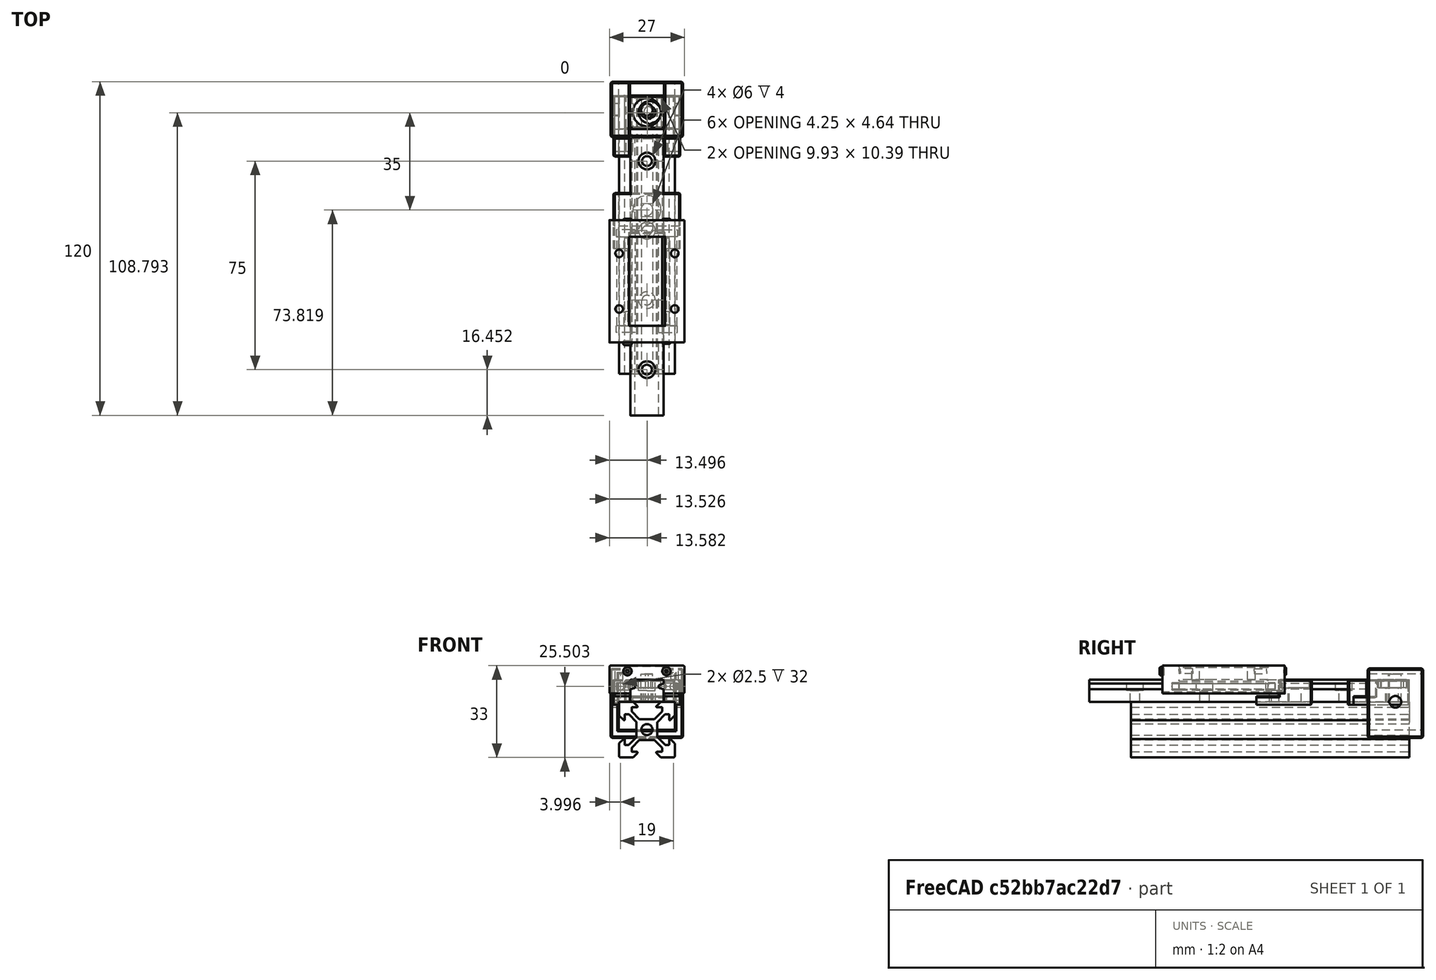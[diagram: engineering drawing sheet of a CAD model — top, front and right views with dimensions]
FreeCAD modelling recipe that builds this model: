
FCSTD DOCUMENT  (FreeCAD 0.18R16146 (Git))
Label: rail-mounter
License: All rights reserved
LicenseURL: http://en.wikipedia.org/wiki/All_rights_reserved
objects: Part::Box×14, Part::Feature×13, Part::Cut×10, Part::Chamfer×8, Part::MultiFuse×8, Part::Cylinder×6
note: 59 computed .brp shape members not serialized (recipe doc carries the construction recipe); baked Part::Feature solids carry a one-line shape summary decoded from their .brp

FEATURE [Part::Box] Box  label="Cube"
  AttacherType = Attacher::AttachEngine3D
  Height = 8
  Length = 24
  Placement = pos=(-12,3,0) rot=(0,0,1;0rad)
  Width = 12
FEATURE [Part::Box] Box001  label="ref"
  AttacherType = Attacher::AttachEngine3D
  Height = 2
  Length = 12.2
  Placement = pos=(-6.1,-5,0) rot=(0,0,1;0rad)
  Width = 4.5
FEATURE [Part::Cylinder] Cylinder
  Angle = 360
  AttacherType = Attacher::AttachEngine3D
  Height = 8
  Placement = pos=(0,7,0) rot=(0,0,1;0rad)
  Radius = 0.5
FEATURE [Part::Feature] Cut001001  label="Cut002"
  shape: bbox 18 x 20 x 8 mm, 17 faces (baked)
FEATURE [Part::Chamfer] Chamfer  label="head-tail"
  Base = -> Cut001001
  Edges = 12 edges r=0.5: [Edge1,Edge3,Edge5,Edge6,Edge7,Edge13,Edge15,Edge16,Edge17,Edge33,Edge34,Edge35]
FEATURE [Part::Box] Box003  label="Cube003"
  AttacherType = Attacher::AttachEngine3D
  Height = 20.2
  Length = 20.2
  Placement = pos=(-10.1,0,-10.1) rot=(0,0,1;0rad)
  Width = 20
FEATURE [Part::Box] Box004  label="Cube004"
  AttacherType = Attacher::AttachEngine3D
  Height = 25
  Length = 26
  Placement = pos=(-13,0,-13) rot=(0,0,1;0rad)
  Width = 20
FEATURE [Part::Box] Box005  label="Cube005"
  AttacherType = Attacher::AttachEngine3D
  Height = 13
  Length = 12.2
  Placement = pos=(-6.1,0,0) rot=(0,0,1;0rad)
  Width = 20
FEATURE [Part::MultiFuse] Fusion002
  Shapes = -> [Box003,Box005]
FEATURE [Part::Cylinder] Cylinder004
  Angle = 360
  AttacherType = Attacher::AttachEngine3D
  Height = 10
  Placement = pos=(0,10,0) rot=(0,0,1;0rad)
  Radius = 2.1
FEATURE [Part::Cylinder] Cylinder005
  Angle = 360
  AttacherType = Attacher::AttachEngine3D
  Height = 10
  Placement = pos=(0,8.1,0) rot=(0,0,1;0rad)
  Radius = 0.5
FEATURE [Part::MultiFuse] Fusion003
  Shapes = -> [Cylinder005,Cylinder004]
FEATURE [Part::Feature] Fusion003001  label="Fusion004"
  Placement = pos=(-6.7,0,-1e-15) rot=(0,-1,0;1.5708rad)
  shape: bbox 10 x 4.5 x 4.2 mm, 9 faces (baked)
FEATURE [Part::Feature] Fusion003002  label="Fusion005"
  Placement = pos=(14.7,0,-5.8e-15) rot=(0,-1,0;1.5708rad)
  shape: bbox 10 x 4.5 x 4.2 mm, 9 faces (baked)
FEATURE [Part::Cut] Cut001002
  Base = -> Box004
  Tool = -> Fusion002
FEATURE [Part::Cut] Cut001003
  Base = -> Cut001002
  Tool = -> Fusion003001
FEATURE [Part::Cut] Cut001004
  Base = -> Cut001003
  Tool = -> Fusion003002
FEATURE [Part::Chamfer] Chamfer002
  Base = -> Cut001004
  Edges = 30 edges r=0.5: [Edge1,Edge2,Edge3,Edge4,Edge8,Edge9,Edge10,Edge11,Edge12,Edge13,Edge14,Edge15,Edge16,Edge17,Edge18,Edge19,Edge20,Edge21,Edge22,Edge23,Edge24,Edge25,Edge26,Edge27,Edge28,Edge29,Edge30,Edge31,Edge38,Edge42]
FEATURE [Part::Cylinder] Cylinder006
  Angle = 360
  AttacherType = Attacher::AttachEngine3D
  Height = 3
  Placement = pos=(0,4.1,5) rot=(0,0,1;0rad)
  Radius = 0.5
FEATURE [Part::Box] Box002  label="Cube002"
  AttacherType = Attacher::AttachEngine3D
  Height = 2
  Length = 24
  Placement = pos=(-12,-5,0) rot=(0,0,1;0rad)
  Width = 20
FEATURE [Part::Cut] Cut
  Base = -> Box002
  Tool = -> Box001
FEATURE [Part::MultiFuse] Fusion
  Shapes = -> [Cut,Box]
FEATURE [Part::Box] Box006  label="Cube006"
  AttacherType = Attacher::AttachEngine3D
  Height = 1
  Length = 1.9
  Placement = pos=(-12,-5,-1) rot=(0,0,1;0rad)
  Width = 20
FEATURE [Part::Box] Box007  label="Cube007"
  AttacherType = Attacher::AttachEngine3D
  Height = 1
  Length = 1.9
  Placement = pos=(10.1,-5,-1) rot=(0,0,1;0rad)
  Width = 20
FEATURE [Part::MultiFuse] Fusion003003
  Shapes = -> [Fusion,Box006,Box007]
FEATURE [Part::Cylinder] Cylinder007
  Angle = 360
  AttacherType = Attacher::AttachEngine3D
  Height = 8
  Placement = pos=(0,9,0) rot=(0,0,1;0rad)
  Radius = 2.15
FEATURE [Part::Cylinder] Cylinder008
  Angle = 360
  AttacherType = Attacher::AttachEngine3D
  Height = 3
  Placement = pos=(0,9,5) rot=(0,0,1;0rad)
  Radius = 5.05
FEATURE [Part::MultiFuse] Fusion003004
  Shapes = -> [Cylinder007,Cylinder008]
FEATURE [Part::Cut] Cut001005
  Base = -> Fusion003003
  Tool = -> Fusion003004
FEATURE [Part::Cut] Cut001006
  Base = -> Cut001005
  Tool = -> Cylinder006
FEATURE [Part::Cut] Cut001007  label="head-align-r1"
  Base = -> Cut001006
  Tool = -> Cylinder
FEATURE [Part::Feature] Cut001007001  label="head-align-r002"
  shape: bbox 24 x 20 x 9 mm, 21 faces (baked)
FEATURE [Part::Chamfer] Chamfer003
  Base = -> Cut001007001
  Edges = 14 edges r=0.4: [Edge3,Edge5,Edge12,Edge17,Edge25,Edge27,Edge28,Edge29,Edge30,Edge38,Edge40,Edge45,Edge47,Edge48]
FEATURE [Part::Feature] Cut001007002  label="head-align-r003"
  shape: bbox 24 x 20 x 9 mm, 37 faces (baked)
FEATURE [Part::Box] Box008  label="Cube008"
  AttacherType = Attacher::AttachEngine3D
  Height = 8
  Length = 24
  Placement = pos=(-12,-0.5,0) rot=(0,0,1;0rad)
  Width = 3.5
FEATURE [Part::MultiFuse] Fusion003005
  Shapes = -> [Box008,Cut001007002]
FEATURE [Part::Feature] Fusion003005001  label="Fusion003006"
  shape: bbox 24 x 20 x 9 mm, 21 faces (baked)
FEATURE [Part::Chamfer] Chamfer005  label="big-head"
  Base = -> Fusion003005001
  Edges = 14 edges r=0.4: [Edge3,Edge5,Edge12,Edge14,Edge23,Edge25,Edge28,Edge29,Edge32,Edge37,Edge39,Edge40,Edge47,Edge48]
FEATURE [Part::Feature] Chamfer003001  label="Chamfer004"
  shape: bbox 24 x 20 x 9 mm, 37 faces (baked)
FEATURE [Part::Feature] Chamfer003002  label="Chamfer005"
  shape: bbox 24 x 20 x 9 mm, 37 faces (baked)
FEATURE [Part::Box] Box009  label="Cube009"
  AttacherType = Attacher::AttachEngine3D
  Height = 10
  Length = 12.2
  Placement = pos=(-6.1,-9.5,0) rot=(0,0,1;0rad)
  Width = 10
FEATURE [Part::Cut] Cut001007003
  Base = -> Chamfer003002
  Placement = pos=(0,-35,0) rot=(0,0,1;0rad)
  Tool = -> Box009
FEATURE [Part::Chamfer] Chamfer003004  label="145"
  Base = -> Cut001007003
  Edges = 5 edges r=0.4: [Edge27,Edge30,Edge31,Edge34,Edge36]
FEATURE [Part::Feature] Chamfer003003001  label="155"
  shape: bbox 24 x 20 x 9 mm, 40 faces (baked)
FEATURE [Part::Box] Box010  label="Cube010"
  AttacherType = Attacher::AttachEngine3D
  Height = 10
  Length = 12.2
  Placement = pos=(-6.1,-7.85,0) rot=(0,0,1;0rad)
  Width = 8
FEATURE [Part::Feature] Cut001007004001  label="Cut001007005"
  shape: bbox 24 x 20 x 9 mm, 39 faces (baked)
FEATURE [Part::Chamfer] Chamfer003003002  label="150"
  Base = -> Cut001007004001
  Edges = 5 edges r=0.4: [Edge27,Edge30,Edge31,Edge34,Edge36]
FEATURE [Part::Cut] Cut001007004002
  Base = -> Chamfer003001
  Tool = -> Box010
FEATURE [Part::Chamfer] Chamfer003003003  label="150-015"
  Base = -> Cut001007004002
  Edges = 5 edges r=0.4: [Edge27,Edge30,Edge31,Edge34,Edge36]
FEATURE [Part::Feature] Chamfer003003003001  label="150-016"
  shape: bbox 24 x 20 x 9 mm, 40 faces (baked)
FEATURE [Part::Box] Box011  label="Cube011"
  AttacherType = Attacher::AttachEngine3D
  Height = 9
  Length = 24
  Placement = pos=(-12,-7,-1) rot=(0,0,1;0rad)
  Width = 10.5
FEATURE [Part::Box] Box012  label="Cube012"
  AttacherType = Attacher::AttachEngine3D
  Height = 1
  Length = 20.2
  Placement = pos=(-10.1,-7,-1) rot=(0,0,1;0rad)
  Width = 10.5
FEATURE [Part::Box] Box013  label="Cube013"
  AttacherType = Attacher::AttachEngine3D
  Height = 15
  Length = 12.2
  Placement = pos=(-6.1,-10.35,-1) rot=(0,0,1;0rad)
  Width = 10.5
FEATURE [Part::MultiFuse] Fusion003005002
  Shapes = -> [Box012,Box013]
FEATURE [Part::Cut] Cut001007004003
  Base = -> Box011
  Tool = -> Fusion003005002
FEATURE [Part::Chamfer] Chamfer003003003002
  Base = -> Cut001007004003
  Edges = 11 edges r=0.4: [Edge1,Edge2,Edge8,Edge9,Edge11,Edge12,Edge13,Edge14,Edge15,Edge30,Edge32]
FEATURE [Part::Feature] Cut036009013017007008008021005005007001  label="MGN12H-pref001"
  Placement = pos=(0.11,-51.5,18) rot=(-0.707107,-0.707107,0;3.14159rad)
  shape: bbox 27 x 100 x 13 mm, 207 faces (baked)
FEATURE [Part::Feature] Part__Feature112001002001  label="2020-extrusion-pred001"
  Placement = pos=(10,15,-20) rot=(0.57735,-0.57735,0.57735;2.0944rad)
  shape: bbox 20 x 100 x 20 mm, 91 faces (baked)
FEATURE [Part::MultiFuse] Fusion003005003  label="bear-mera-ext-block-mount"
  Shapes = -> [Chamfer003003003002,Chamfer003003003001]
